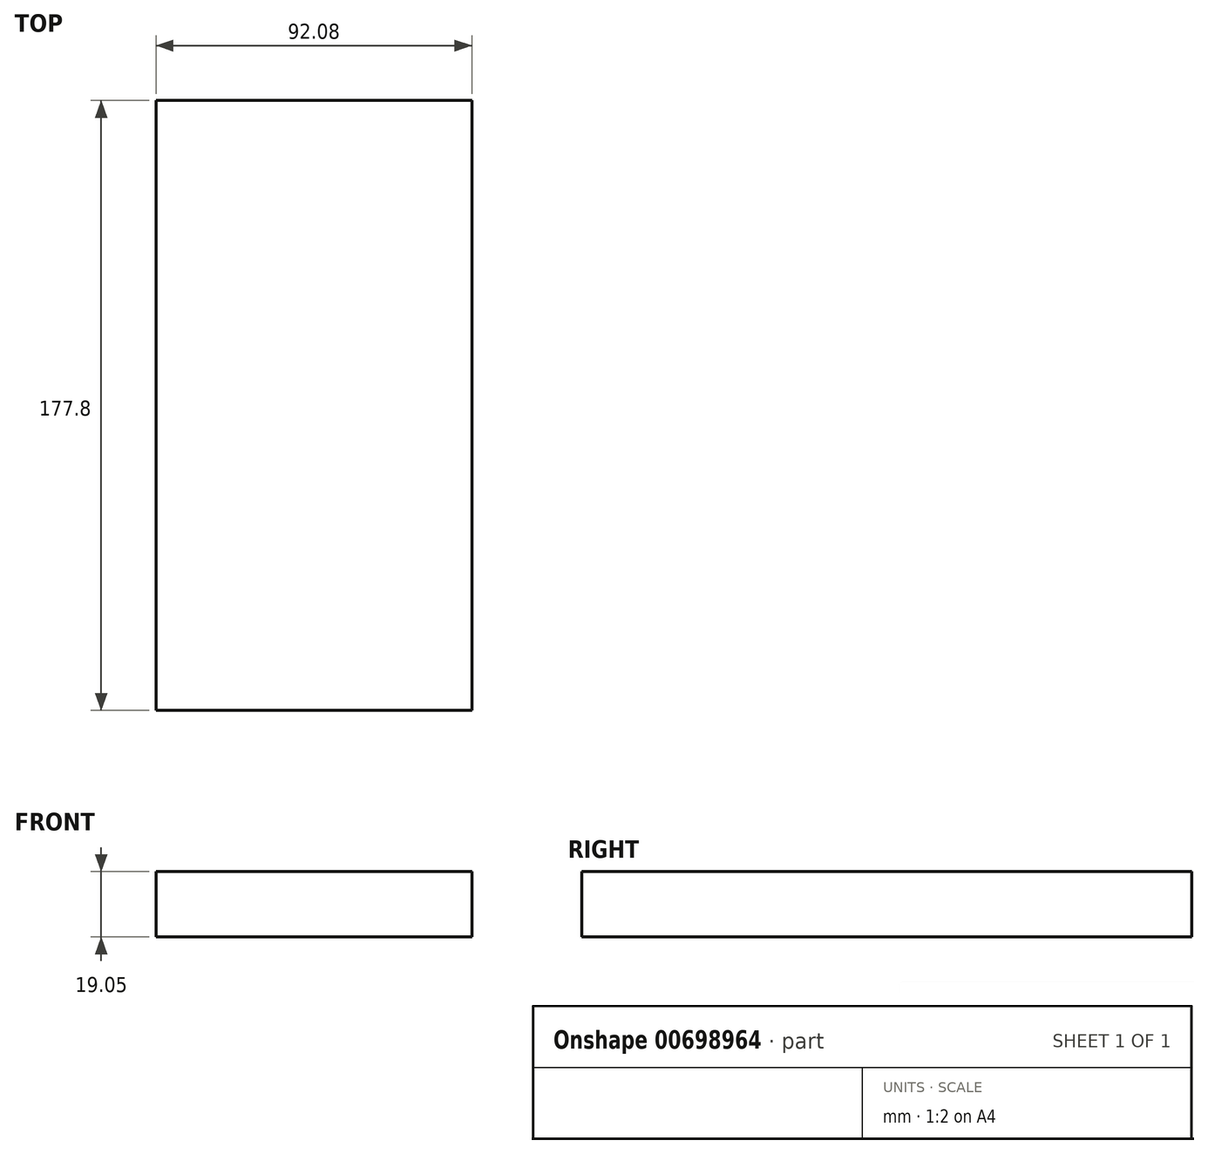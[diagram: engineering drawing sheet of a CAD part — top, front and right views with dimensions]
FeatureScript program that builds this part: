
annotation { "Feature Type Name" : "Feature", "Feature Type Description" : "" }
export const myFeature = defineFeature(function(context is Context, id is Id, definition is map)
    precondition{}
    {
        {
            var Q0;
            Q0=qCreatedBy(makeId("Front.planeOp"),FACE);
            var sketch = newSketch(context, id + "F0", { "sketchPlane" : qUnion([Q0])});
            skLineSegment(sketch, "E0.bottom", {"start": v(0, 0) * mm, "end": v(92.08, 0) * mm});
            skLineSegment(sketch, "E0.top", {"start": v(0, 19.05) * mm, "end": v(92.08, 19.05) * mm});
            skLineSegment(sketch, "E0.left", {"start": v(0, 0) * mm, "end": v(0, 19.05) * mm});
            skLineSegment(sketch, "E0.right", {"start": v(92.08, 0) * mm, "end": v(92.08, 19.05) * mm});
            skSolve(sketch);
        }
        {
            var Q0;
            Q0=qSketchRegion(id+"F0",true);
            extrude(context, id + "F1", {"entities" : qUnion([Q0]), "oppositeDirection" : true, "depth" : 177.8 * mm, "offsetDistance" : 25.4 * mm});
        }
    });
